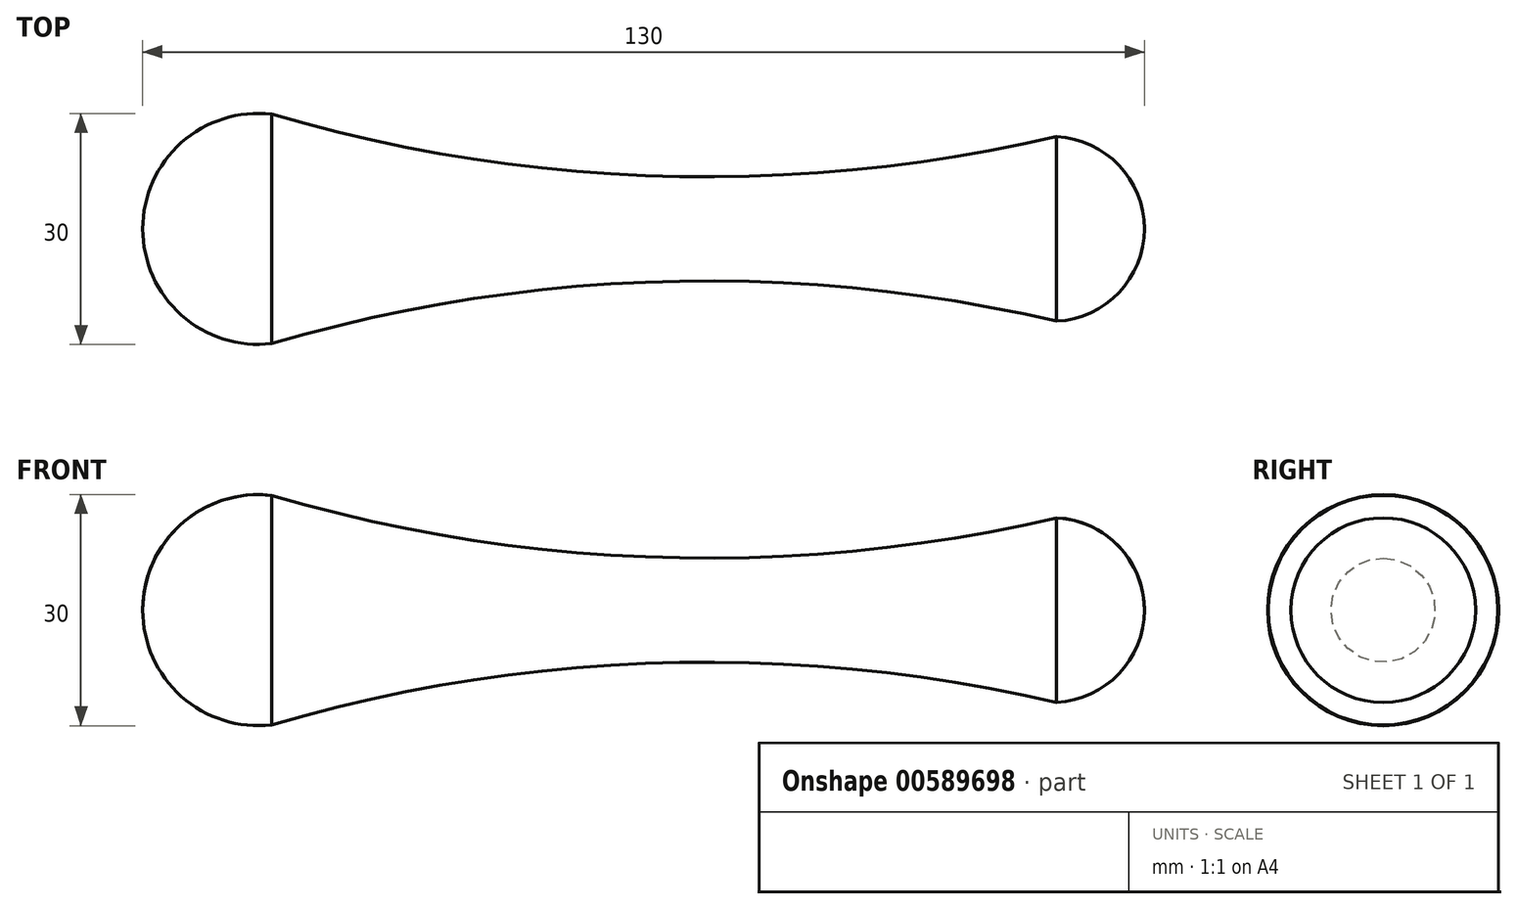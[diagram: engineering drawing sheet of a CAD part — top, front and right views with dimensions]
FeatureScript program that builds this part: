
annotation { "Feature Type Name" : "Feature", "Feature Type Description" : "" }
export const myFeature = defineFeature(function(context is Context, id is Id, definition is map)
    precondition{}
    {
        {
            var Q0;
            Q0=qCreatedBy(makeId("Front.planeOp"),FACE);
            var sketch = newSketch(context, id + "F0", { "sketchPlane" : qUnion([Q0])});
            skLineSegment(sketch, "E0", {"start": v(-62.61, 0) * mm, "end": v(67.39, 0) * mm});
            skArc(sketch, "E1", {"start": v(-62.61, 0) * mm, "mid": v(-57.59, 11.2) * mm, "end": v(-45.89, 14.9) * mm});
            skArc(sketch, "E2", {"start": v(67.39, 0) * mm, "mid": v(64.1, 8.26) * mm, "end": v(56.02, 11.98) * mm});
            skArc(sketch, "E3", {"start": v(-45.89, 14.9) * mm, "mid": v(4.88, 6.84) * mm, "end": v(56.02, 11.98) * mm});
            skSolve(sketch);
        }
        {
            var Q0;
            Q0=makeQuery(id+"F0.imprint","IMPRINT",FACE,{"disambiguationData":[TD([[makeQuery(id+"F0.imprint","IMPRINT",EDGE,{"derivedFrom":sQuery(id+"F0.wireOp",EDGE,"E0")}),1.0]])]});
            var Q1;
            Q1=sQuery(id+"F0.wireOp",EDGE,"E0");
            revolve(context, id + "F1", {"entities" : qUnion([Q0]), "axis" : qUnion([Q1]), "revolveType" : RevolveType.FULL});
        }
    });
